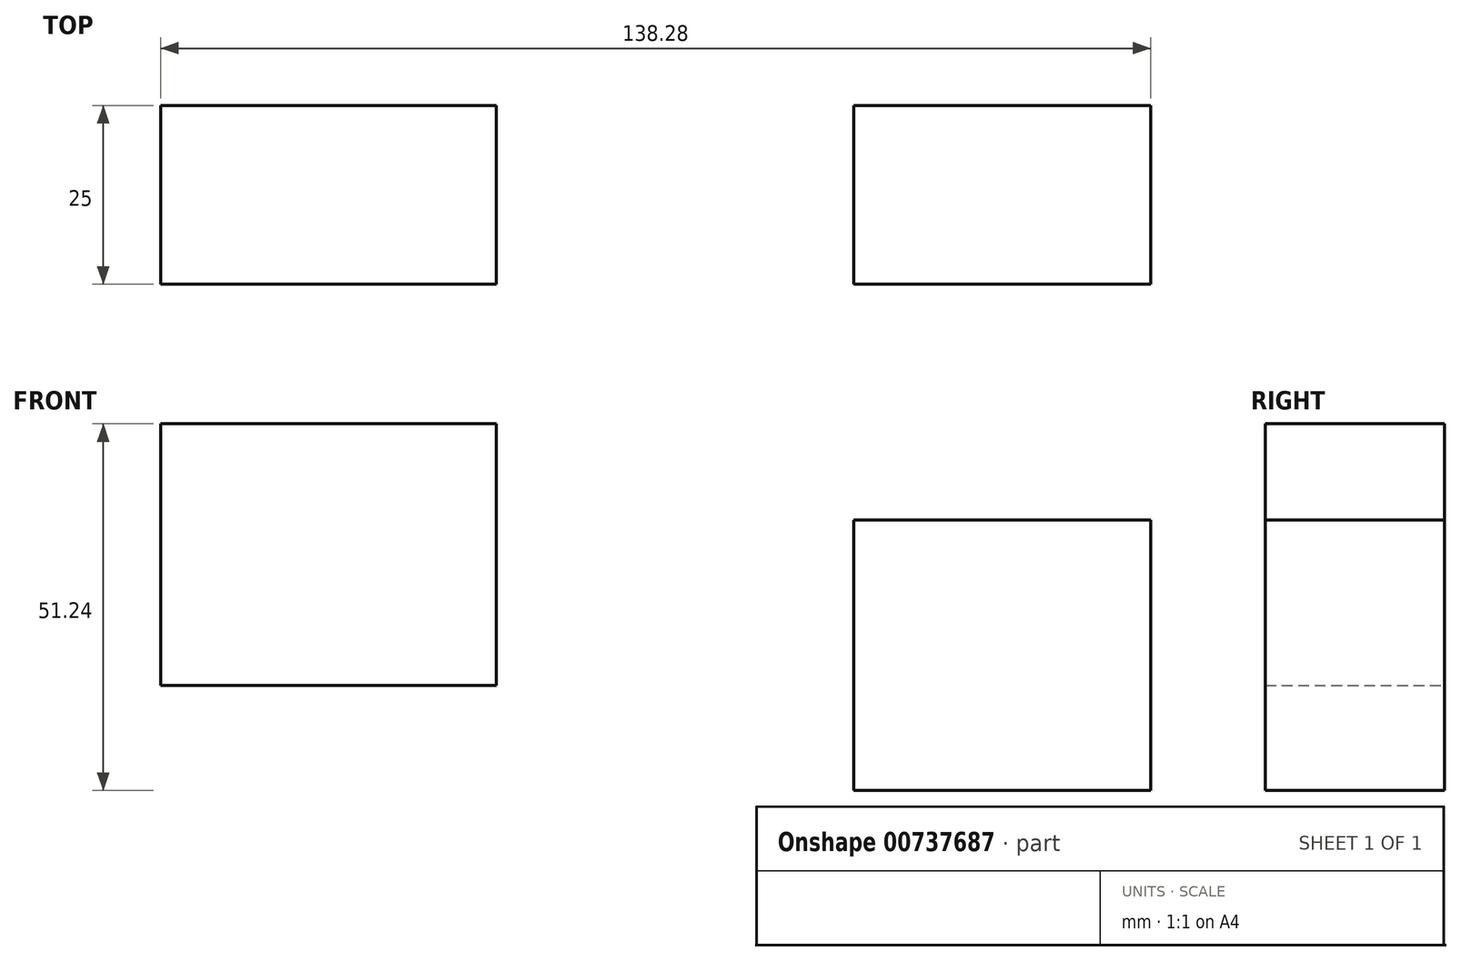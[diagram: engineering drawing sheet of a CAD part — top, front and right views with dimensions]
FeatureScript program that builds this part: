
annotation { "Feature Type Name" : "Feature", "Feature Type Description" : "" }
export const myFeature = defineFeature(function(context is Context, id is Id, definition is map)
    precondition{}
    {
        {
            var Q0;
            Q0=qCreatedBy(makeId("Front.planeOp"),FACE);
            var sketch = newSketch(context, id + "F0", { "sketchPlane" : qUnion([Q0])});
            skLineSegment(sketch, "E0.bottom", {"start": v(-125.32, 14.7) * mm, "end": v(-78.4, 14.7) * mm});
            skLineSegment(sketch, "E0.top", {"start": v(-125.32, 51.24) * mm, "end": v(-78.4, 51.24) * mm});
            skLineSegment(sketch, "E0.left", {"start": v(-125.32, 14.7) * mm, "end": v(-125.32, 51.24) * mm});
            skLineSegment(sketch, "E0.right", {"start": v(-78.4, 14.7) * mm, "end": v(-78.4, 51.24) * mm});
            skPoint(sketch, "E0.middle", {"position": v(-101.86, 32.97) * mm});
            skLineSegment(sketch, "E1.bottom", {"start": v(-28.52, 0) * mm, "end": v(12.96, 0) * mm});
            skLineSegment(sketch, "E1.top", {"start": v(-28.52, 37.78) * mm, "end": v(12.96, 37.78) * mm});
            skLineSegment(sketch, "E1.left", {"start": v(-28.52, 0) * mm, "end": v(-28.52, 37.78) * mm});
            skLineSegment(sketch, "E1.right", {"start": v(12.96, 0) * mm, "end": v(12.96, 37.78) * mm});
            skPoint(sketch, "E1.middle", {"position": v(-7.78, 18.9) * mm});
            skSolve(sketch);
        }
        {
            var Q0;
            Q0=makeQuery(id+"F0.imprint","IMPRINT",FACE,{"disambiguationData":[TD([[makeQuery(id+"F0.imprint","IMPRINT",EDGE,{"derivedFrom":sQuery(id+"F0.wireOp",EDGE,"E0.bottom")}),1.0]])]});
            var Q1;
            Q1=makeQuery(id+"F0.imprint","IMPRINT",FACE,{"disambiguationData":[TD([[makeQuery(id+"F0.imprint","IMPRINT",EDGE,{"derivedFrom":sQuery(id+"F0.wireOp",EDGE,"E1.bottom")}),1.0]])]});
            extrude(context, id + "F1", {"entities" : qUnion([Q0, Q1]), "depth" : 25 * mm, "offsetDistance" : 25 * mm});
        }
    });
